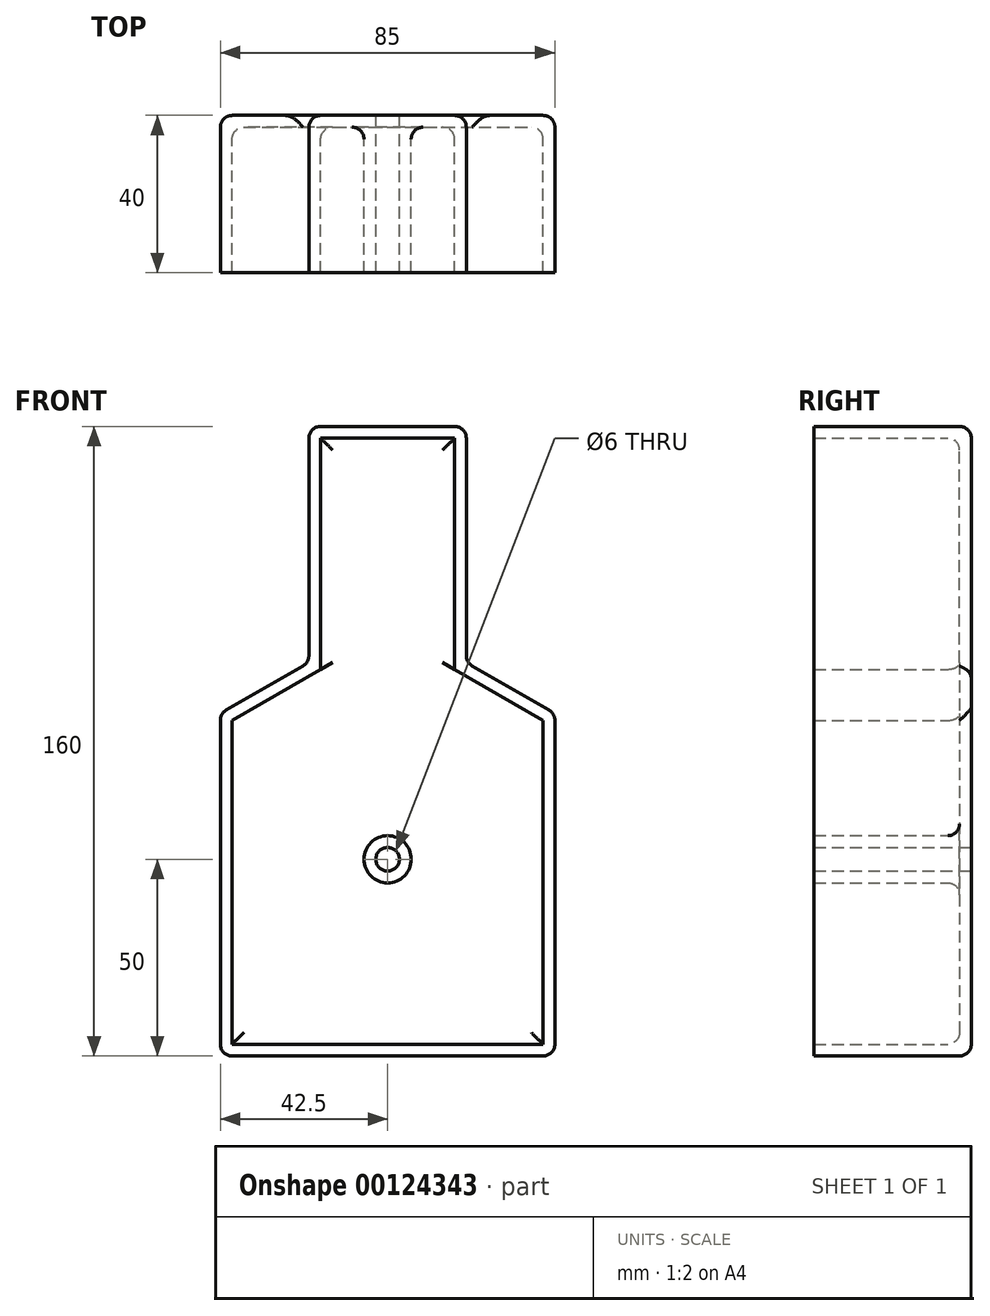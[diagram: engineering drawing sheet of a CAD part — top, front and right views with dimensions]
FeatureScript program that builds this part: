
annotation { "Feature Type Name" : "Feature", "Feature Type Description" : "" }
export const myFeature = defineFeature(function(context is Context, id is Id, definition is map)
    precondition{}
    {
        {
            var Q0;
            Q0=qCreatedBy(makeId("Front.planeOp"),FACE);
            var sketch = newSketch(context, id + "F0", { "sketchPlane" : qUnion([Q0])});
            skLineSegment(sketch, "E0", {"start": v(-94.03, 0) * mm, "end": v(93.65, 0) * mm, "construction": true});
            skLineSegment(sketch, "E1", {"start": v(-99.55, 50) * mm, "end": v(103.1, 50) * mm, "construction": true});
            skLineSegment(sketch, "E2", {"start": v(-99.55, 100) * mm, "end": v(86.15, 100) * mm, "construction": true});
            skLineSegment(sketch, "E3", {"start": v(0, -39.1) * mm, "end": v(0, 100) * mm, "construction": true});
            skSolve(sketch);
        }
        {
            var Q0;
            Q0=qCreatedBy(makeId("Front.planeOp"),FACE);
            var sketch = newSketch(context, id + "F1", { "sketchPlane" : qUnion([Q0])});
            skLineSegment(sketch, "E4.right", {"start": v(20, 50) * mm, "end": v(20, 110) * mm});
            skLineSegment(sketch, "E5.right", {"start": v(-20, 50) * mm, "end": v(-20, 110) * mm});
            skLineSegment(sketch, "E6", {"start": v(42.5, 37) * mm, "end": v(42.5, -50) * mm});
            skLineSegment(sketch, "E7", {"start": v(-42.5, 37) * mm, "end": v(-42.5, -50) * mm});
            skLineSegment(sketch, "E8", {"start": v(-42.5, -50) * mm, "end": v(42.5, -50) * mm});
            skLineSegment(sketch, "E9", {"start": v(-20, 110) * mm, "end": v(20, 110) * mm});
            skCircle(sketch, "E10", {"center": v(0, 0) * mm, "radius": 3 * mm});
            skLineSegment(sketch, "E11", {"start": v(-20, 50) * mm, "end": v(20, 50) * mm, "construction": true});
            skLineSegment(sketch, "E12", {"start": v(-20, 50) * mm, "end": v(-42.5, 37) * mm});
            skLineSegment(sketch, "E13", {"start": v(20, 50) * mm, "end": v(42.5, 37) * mm});
            skSolve(sketch);
        }
        {
            var Q0;
            Q0 = qSketchRegion(id + "F1", true);
            extrude(context, id + "F2", {"entities" : qUnion([Q0]), "depth" : 40 * mm});
        }
        {
            var Q0;
            Q0=makeQuery(id+"F2.opExtrude","CAP_FACE",FACE,{"disambiguationData":[OSD([sQuery(id+"F1.wireOp",EDGE,"E4.right"),sQuery(id+"F1.wireOp",EDGE,"E5.right"),sQuery(id+"F1.wireOp",EDGE,"6WuVQe2u-cMzT-iPQM-N49p-9YHfXahXi2i3"),sQuery(id+"F1.wireOp",EDGE,"TCMM6Tzc-pCFV-Q7wZ-l0O0-wWKHVzFUVLzV"),sQuery(id+"F1.wireOp",EDGE,"E6"),sQuery(id+"F1.wireOp",EDGE,"E7"),sQuery(id+"F1.wireOp",EDGE,"E8"),sQuery(id+"F1.wireOp",EDGE,"E9")])],"isStart":false});
            shell(context, id + "F3", {"entities" : qUnion([Q0]), "thickness" : 3 * mm});
        }
        {
            var Q0;
            {var subQ0=sQuery(id+"F1.wireOp",EDGE,"TCMM6Tzc-pCFV-Q7wZ-l0O0-wWKHVzFUVLzV");Q0=makeQuery(id+"F3.opShell","OFFSET_EDGE",EDGE,{"disambiguationData":[OSD([subQ0]),TDD([makeQuery(id+"F2.opExtrude","CAP_EDGE",EDGE,{"disambiguationData":[OSD([subQ0])],"isStart":true})])]});}
            var Q1;
            {var subQ0=sQuery(id+"F1.wireOp",EDGE,"6WuVQe2u-cMzT-iPQM-N49p-9YHfXahXi2i3");Q1=makeQuery(id+"F3.opShell","OFFSET_EDGE",EDGE,{"disambiguationData":[OSD([subQ0]),TDD([makeQuery(id+"F2.opExtrude","CAP_EDGE",EDGE,{"disambiguationData":[OSD([subQ0])],"isStart":true})])]});}
            var Q2;
            {var subQ0=sQuery(id+"F1.wireOp",EDGE,"E6");Q2=makeQuery(id+"F3.opShell","OFFSET_EDGE",EDGE,{"disambiguationData":[OSD([subQ0]),TDD([makeQuery(id+"F2.opExtrude","CAP_EDGE",EDGE,{"disambiguationData":[OSD([subQ0])],"isStart":true})])]});}
            var Q3;
            {var subQ0=sQuery(id+"F1.wireOp",EDGE,"E8");Q3=makeQuery(id+"F3.opShell","OFFSET_EDGE",EDGE,{"disambiguationData":[OSD([subQ0]),TDD([makeQuery(id+"F2.opExtrude","CAP_EDGE",EDGE,{"disambiguationData":[OSD([subQ0])],"isStart":true})])]});}
            var Q4;
            {var subQ0=sQuery(id+"F1.wireOp",EDGE,"E7");Q4=makeQuery(id+"F3.opShell","OFFSET_EDGE",EDGE,{"disambiguationData":[OSD([subQ0]),TDD([makeQuery(id+"F2.opExtrude","CAP_EDGE",EDGE,{"disambiguationData":[OSD([subQ0])],"isStart":true})])]});}
            var Q5;
            {var subQ0=sQuery(id+"F1.wireOp",EDGE,"E4.right");Q5=makeQuery(id+"F3.opShell","OFFSET_EDGE",EDGE,{"disambiguationData":[OSD([subQ0]),TDD([makeQuery(id+"F2.opExtrude","CAP_EDGE",EDGE,{"disambiguationData":[OSD([subQ0])],"isStart":true})])]});}
            var Q6;
            {var subQ0=sQuery(id+"F1.wireOp",EDGE,"E9");Q6=makeQuery(id+"F3.opShell","OFFSET_EDGE",EDGE,{"disambiguationData":[OSD([subQ0]),TDD([makeQuery(id+"F2.opExtrude","CAP_EDGE",EDGE,{"disambiguationData":[OSD([subQ0])],"isStart":true})])]});}
            var Q7;
            {var subQ0=sQuery(id+"F1.wireOp",EDGE,"E5.right");Q7=makeQuery(id+"F3.opShell","OFFSET_EDGE",EDGE,{"disambiguationData":[OSD([subQ0]),TDD([makeQuery(id+"F2.opExtrude","CAP_EDGE",EDGE,{"disambiguationData":[OSD([subQ0])],"isStart":true})])]});}
            var Q8;
            Q8=makeQuery(id+"F2.opExtrude","SWEPT_EDGE",EDGE,{"disambiguationData":[OSD([sQuery(id+"F1.wireOp",EDGE,"E5.right"),sQuery(id+"F1.wireOp",EDGE,"6WuVQe2u-cMzT-iPQM-N49p-9YHfXahXi2i3")])]});
            var Q9;
            Q9=makeQuery(id+"F2.opExtrude","SWEPT_EDGE",EDGE,{"disambiguationData":[OSD([sQuery(id+"F1.wireOp",EDGE,"6WuVQe2u-cMzT-iPQM-N49p-9YHfXahXi2i3"),sQuery(id+"F1.wireOp",EDGE,"E7")])]});
            var Q10;
            Q10=makeQuery(id+"F2.opExtrude","SWEPT_EDGE",EDGE,{"disambiguationData":[OSD([sQuery(id+"F1.wireOp",EDGE,"E5.right"),sQuery(id+"F1.wireOp",EDGE,"E9")])]});
            var Q11;
            Q11=makeQuery(id+"F2.opExtrude","SWEPT_EDGE",EDGE,{"disambiguationData":[OSD([sQuery(id+"F1.wireOp",EDGE,"E4.right"),sQuery(id+"F1.wireOp",EDGE,"E9")])]});
            var Q12;
            Q12=makeQuery(id+"F2.opExtrude","SWEPT_EDGE",EDGE,{"disambiguationData":[OSD([sQuery(id+"F1.wireOp",EDGE,"E4.right"),sQuery(id+"F1.wireOp",EDGE,"TCMM6Tzc-pCFV-Q7wZ-l0O0-wWKHVzFUVLzV")])]});
            var Q13;
            Q13=makeQuery(id+"F2.opExtrude","SWEPT_EDGE",EDGE,{"disambiguationData":[OSD([sQuery(id+"F1.wireOp",EDGE,"TCMM6Tzc-pCFV-Q7wZ-l0O0-wWKHVzFUVLzV"),sQuery(id+"F1.wireOp",EDGE,"E6")])]});
            var Q14;
            Q14=makeQuery(id+"F2.opExtrude","SWEPT_EDGE",EDGE,{"disambiguationData":[OSD([sQuery(id+"F1.wireOp",EDGE,"E6"),sQuery(id+"F1.wireOp",EDGE,"E8")])]});
            var Q15;
            Q15=makeQuery(id+"F2.opExtrude","SWEPT_EDGE",EDGE,{"disambiguationData":[OSD([sQuery(id+"F1.wireOp",EDGE,"E7"),sQuery(id+"F1.wireOp",EDGE,"E8")])]});
            var Q16;
            Q16=makeQuery(id+"F2.opExtrude","CAP_EDGE",EDGE,{"disambiguationData":[OSD([sQuery(id+"F1.wireOp",EDGE,"E9")])],"isStart":true});
            var Q17;
            Q17=makeQuery(id+"F2.opExtrude","CAP_EDGE",EDGE,{"disambiguationData":[OSD([sQuery(id+"F1.wireOp",EDGE,"E4.right")])],"isStart":true});
            var Q18;
            Q18=makeQuery(id+"F2.opExtrude","CAP_EDGE",EDGE,{"disambiguationData":[OSD([sQuery(id+"F1.wireOp",EDGE,"E7")])],"isStart":true});
            var Q19;
            Q19=makeQuery(id+"F2.opExtrude","CAP_EDGE",EDGE,{"disambiguationData":[OSD([sQuery(id+"F1.wireOp",EDGE,"E5.right")])],"isStart":true});
            var Q20;
            Q20=makeQuery(id+"F2.opExtrude","CAP_EDGE",EDGE,{"disambiguationData":[OSD([sQuery(id+"F1.wireOp",EDGE,"E8")])],"isStart":true});
            var Q21;
            Q21=makeQuery(id+"F2.opExtrude","CAP_EDGE",EDGE,{"disambiguationData":[OSD([sQuery(id+"F1.wireOp",EDGE,"E6")])],"isStart":true});
            var Q22;
            {var subQ0=sQuery(id+"F1.wireOp",EDGE,"E10");Q22=makeQuery(id+"F3.opShell","OFFSET_EDGE",EDGE,{"disambiguationData":[OSD([subQ0]),TDD([makeQuery(id+"F2.opExtrude","CAP_EDGE",EDGE,{"disambiguationData":[OSD([subQ0])],"isStart":true})])]});}
            fillet(context, id + "F4", {"entities" : qUnion([Q0, Q1, Q2, Q3, Q4, Q5, Q6, Q7, Q8, Q9, Q10, Q11, Q12, Q13, Q14, Q15, Q16, Q17, Q18, Q19, Q20, Q21, Q22]), "radius" : 3 * mm, "tangentPropagation" : true, "allowEdgeOverflow" : false});
        }
    });
